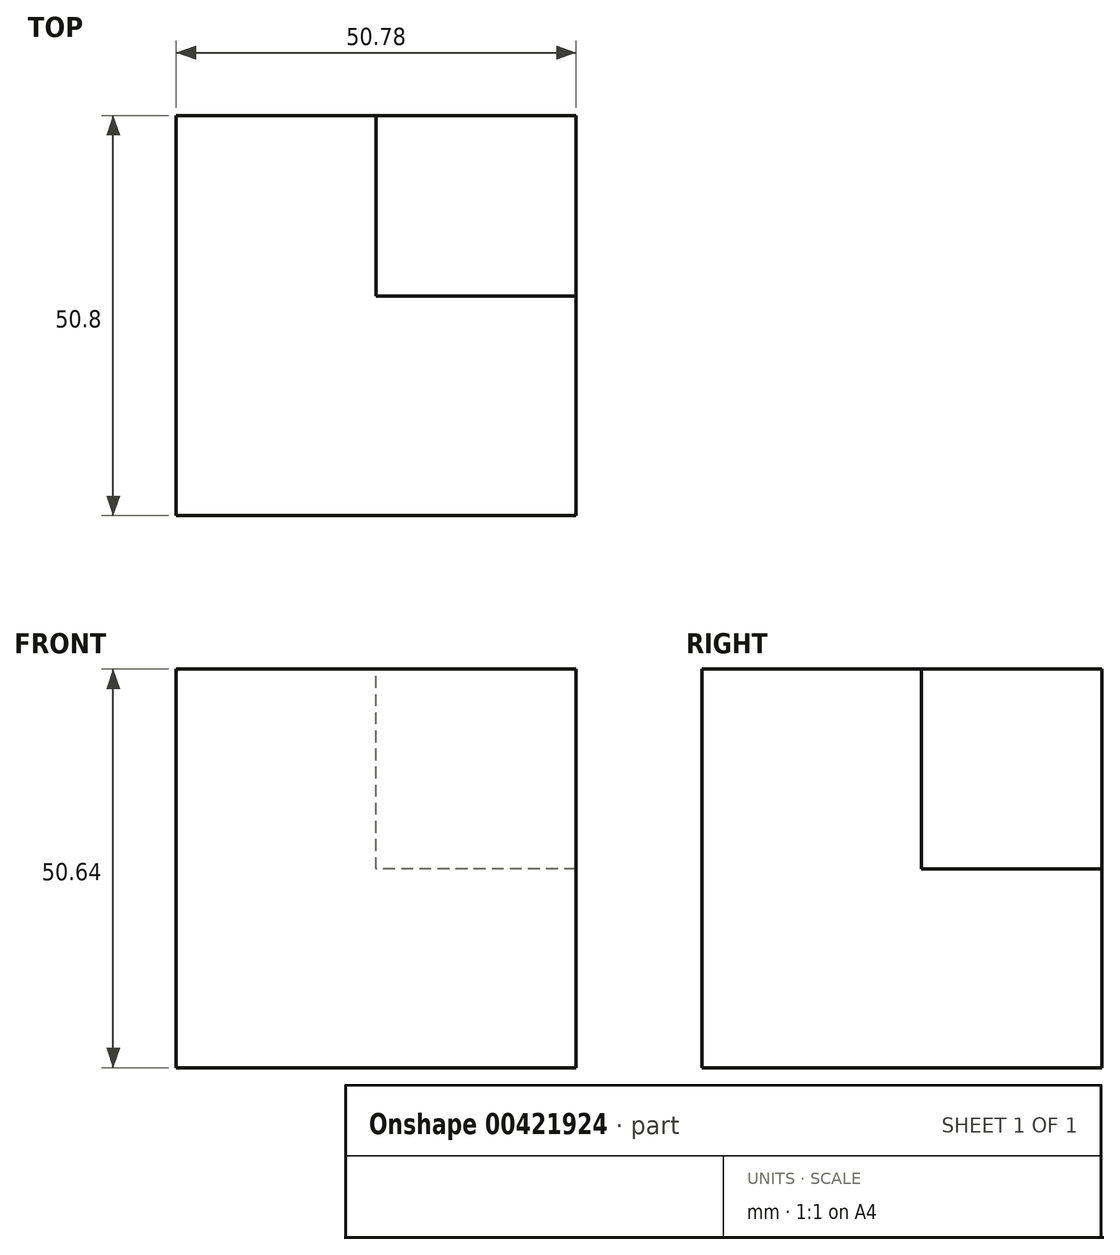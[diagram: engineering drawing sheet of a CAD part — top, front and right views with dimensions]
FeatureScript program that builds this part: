
annotation { "Feature Type Name" : "Feature", "Feature Type Description" : "" }
export const myFeature = defineFeature(function(context is Context, id is Id, definition is map)
    precondition{}
    {
        {
            var Q0;
            Q0=qCreatedBy(makeId("Front.planeOp"),FACE);
            var sketch = newSketch(context, id + "F0", { "sketchPlane" : qUnion([Q0])});
            skLineSegment(sketch, "E0", {"start": v(28.27, 0) * mm, "end": v(-22.5, 0) * mm});
            skLineSegment(sketch, "E1", {"start": v(28.27, 0) * mm, "end": v(28.27, 50.64) * mm});
            skLineSegment(sketch, "E2", {"start": v(28.27, 50.64) * mm, "end": v(-22.5, 50.64) * mm});
            skLineSegment(sketch, "E3", {"start": v(-22.5, 50.64) * mm, "end": v(-22.5, 0) * mm});
            skSolve(sketch);
        }
        {
            var Q0;
            Q0 = qSketchRegion(id + "F0", true);
            extrude(context, id + "F1", {"entities" : qUnion([Q0]), "depth" : 50.8 * mm});
        }
        {
            var Q0;
            Q0=makeQuery(id+"F1.opExtrude","SWEPT_FACE",FACE,{"disambiguationData":[OSD([sQuery(id+"F0.wireOp",EDGE,"E2")])]});
            var sketch = newSketch(context, id + "F2", { "sketchPlane" : qUnion([Q0])});
            skLineSegment(sketch, "E4", {"start": v(28.27, 0) * mm, "end": v(2.88, 0) * mm});
            skLineSegment(sketch, "E5", {"start": v(2.88, 0) * mm, "end": v(2.88, -22.92) * mm});
            skLineSegment(sketch, "E6", {"start": v(2.88, -22.92) * mm, "end": v(28.27, -22.92) * mm});
            skSolve(sketch);
        }
        {
            var Q0;
            {var subQ0=sQuery(id+"F2.wireOp",EDGE,"E4");Q0=makeQuery(id+"F2.imprint","IMPRINT",FACE,{"disambiguationData":[TD([[makeQuery(id+"F2.imprint","IMPRINT",EDGE,{"derivedFrom":subQ0}),1.0]])]});}
            extrude(context, id + "F3", {"entities" : qUnion([Q0]), "operationType" : NewBodyOperationType.REMOVE, "oppositeDirection" : true, "depth" : 25.4 * mm});
        }
    });
